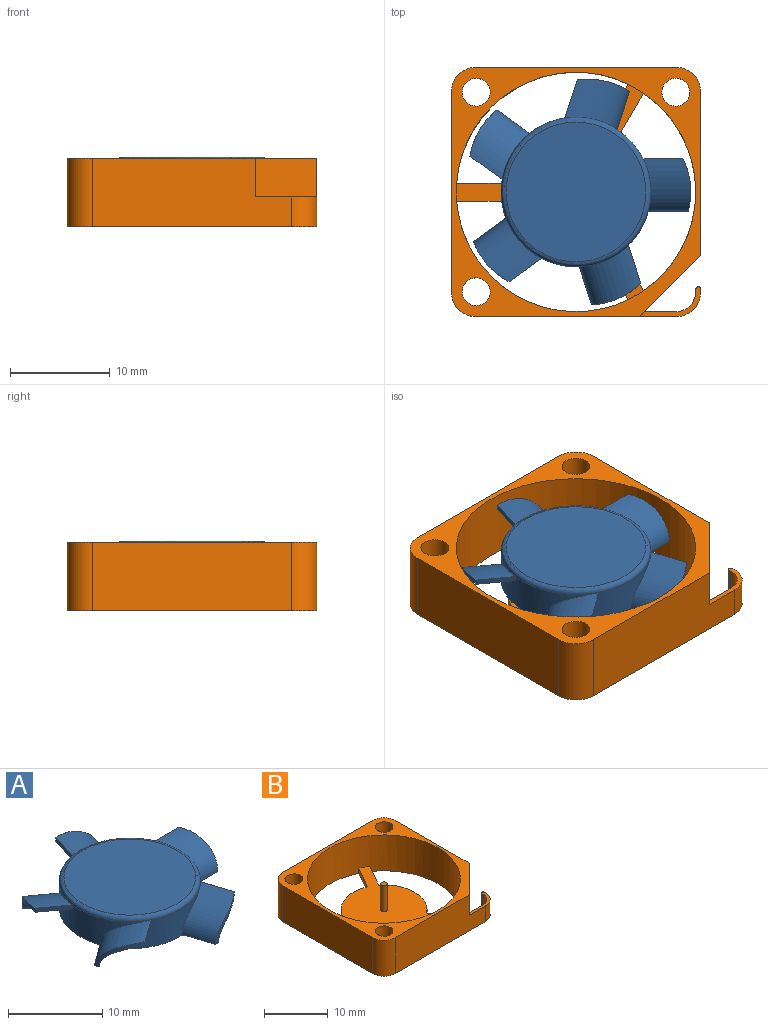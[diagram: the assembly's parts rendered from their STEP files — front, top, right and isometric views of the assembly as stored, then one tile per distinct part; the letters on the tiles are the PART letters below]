
ASSEMBLY  parts=2 mates=1
PART A: 31 faces, bbox 22.1x22.6x4 mm
  f0: cylinder r=6.5mm len=13mm, axis (0,0,-1), area 122.5mm2, adj f24,f25
  f1: torus R=7mm, axis (0,0,1), area 36.1mm2, adj f2,f23
  f2: cylinder r=7.5mm len=15mm, axis (0,0,-1), area 148.3mm2, adj f1,f3,f4,f6,f7,f8,f9,f11
  f3: plane 3.84x1.75mm, normal (0,0,-1), area 2mm2, adj f2,f5,f6,f7
  f4: plane 3.8x1.24mm, normal (0.95,0.31,0), area 2mm2, adj f2,f5,f6,f7
  f5: cylinder r=7.5mm len=4.92mm, axis (0,0,-1), area 3.3mm2, adj f3,f4,f6,f7
  f6: bspline ~5.96x5.66mm, area 24.4mm2, adj f2,f3,f4,f5
  f7: bspline ~6.16x5.94mm, area 27.6mm2, adj f2,f3,f4,f5
  f8: plane 3.43x2.83mm, normal (0,0,-1), area 2mm2, adj f2,f10,f11,f12
  f9: plane 3.24x2.35mm, normal (0.59,-0.81,0), area 2mm2, adj f2,f10,f11,f12
  f10: cylinder r=7.5mm len=4.02mm, axis (0,0,-1), area 3.3mm2, adj f8,f9,f11,f12
  f11: bspline ~6.65x5.93mm, area 24.4mm2, adj f2,f8,f9,f10
  f12: bspline ~6.79x6.37mm, area 27.6mm2, adj f2,f8,f9,f10
  f13: plane 3.63x2.69mm, normal (0,0,-1), area 2mm2, adj f2,f15,f16,f17
  f14: plane 3.24x2.35mm, normal (-0.59,-0.81,0), area 2mm2, adj f2,f15,f16,f17
  f15: cylinder r=7.5mm len=4.62mm, axis (0,0,-1), area 3.3mm2, adj f13,f14,f16,f17
  f16: bspline ~6.64x5.57mm, area 24.4mm2, adj f2,f13,f14,f15
  f17: bspline ~6.98x5.96mm, area 27.6mm2, adj f2,f13,f14,f15
  f18: plane 4.07x1.67mm, normal (0,0,-1), area 2mm2, adj f2,f20,f21,f22
  f19: plane 3.8x1.24mm, normal (-0.95,0.31,0), area 2mm2, adj f2,f20,f21,f22
  f20: cylinder r=7.5mm len=5.24mm, axis (0,0,-1), area 3.3mm2, adj f18,f19,f21,f22
  f21: bspline ~6.04x4.78mm, area 24.4mm2, adj f2,f18,f19,f20
  f22: bspline ~6.48x5.07mm, area 27.6mm2, adj f2,f18,f19,f20
  f23: plane 14x14mm, normal (0,0,1), area 153.9mm2, adj f1
  f24: plane 15x15mm, normal (0,0,-1), area 44mm2, adj f0,f2
  f25: plane 13x13mm, normal (0,0,-1), area 132.7mm2, adj f0
  f26: bspline ~5.34x4.79mm, area 27.6mm2, adj f2,f28,f29,f30
  f27: bspline ~4.84x4.82mm, area 24.4mm2, adj f2,f28,f29,f30
  f28: plane 4x0.5mm, normal (0,1,0), area 2mm2, adj f2,f26,f27,f30
  f29: plane 4.12x0.5mm, normal (0,0,-1), area 2mm2, adj f2,f26,f27,f30
  f30: cylinder r=7.5mm len=5.34mm, axis (0,0,-1), area 3.3mm2, adj f26,f27,f28,f29
PART B: 33 faces, bbox 25x25x6.9 mm
  f0: cylinder r=0.5mm len=5mm, axis (0,0,-1), area 15.7mm2, adj f7,f32
  f1: cylinder r=6.75mm len=9.26mm, axis (0,0,-1), area 12.3mm2, adj f7,f10,f30,f31
  f2: cylinder r=0.25mm len=3mm, axis (0,0,-1), area 2.4mm2, adj f10,f19,f21,f22
  f3: cylinder r=1.4mm len=6.9mm, axis (0,0,-1), area 60.7mm2, adj f9,f10
  f4: cylinder r=1.4mm len=6.9mm, axis (0,0,-1), area 60.7mm2, adj f9,f10
  f5: cylinder r=1.4mm len=6.9mm, axis (0,0,-1), area 60.7mm2, adj f9,f10
  f6: cylinder r=12mm len=24mm, axis (0,0,-1), area 514.8mm2, adj f7,f9,f10,f24,f26,f27,f29,f30
  f7: plane 21.63x18.76mm, normal (0,0,1), area 170.8mm2, adj f0,f1,f6,f24,f25,f26,f27,f28
  f8: plane 6.9x6.12mm, normal (0.71,-0.71,0), area 57.6mm2, adj f9,f10,f12,f13,f18,f19
  f9: plane 25x25mm, normal (0,0,1), area 131.4mm2, adj f3,f4,f5,f6,f8,f11,f12,f13
  f10: plane 25x25mm, normal (0,0,-1), area 306.6mm2, adj f1,f2,f3,f4,f5,f6,f8,f11
  f11: cylinder r=2.5mm len=6.9mm, axis (0,0,-1), area 27.1mm2, adj f9,f10,f12,f17
  f12: plane 20x6.9mm, normal (0,-1,0), area 123.9mm2, adj f8,f9,f10,f11,f19,f20
  f13: plane 16.38x6.9mm, normal (1,0,0), area 113mm2, adj f8,f9,f10,f14
  f14: cylinder r=2.5mm len=6.9mm, axis (0,0,-1), area 27.1mm2, adj f9,f10,f13,f15
  f15: plane 20x6.9mm, normal (0,1,0), area 138mm2, adj f9,f10,f14,f16
  f16: cylinder r=2.5mm len=6.9mm, axis (0,0,-1), area 27.1mm2, adj f9,f10,f15,f17
  f17: plane 20x6.9mm, normal (-1,0,0), area 138mm2, adj f9,f10,f11,f16
  f18: plane 3.12x3mm, normal (0,1,0), area 9.4mm2, adj f8,f10,f19,f23
  f19: plane 6.12x3mm, normal (0,0,1), area 3.7mm2, adj f2,f8,f12,f18,f20,f21,f22,f23
  f20: cylinder r=2.5mm len=3mm, axis (0,0,-1), area 11.8mm2, adj f10,f12,f19,f21
  f21: plane 3x0.25mm, normal (1,0,0), area 0.8mm2, adj f2,f10,f19,f20
  f22: plane 3x0.25mm, normal (-1,0,0), area 0.8mm2, adj f2,f10,f19,f23
  f23: cylinder r=2mm len=3mm, axis (0,0,-1), area 9.4mm2, adj f10,f18,f19,f22
  f24: plane 5.28x1mm, normal (0,-1,0), area 5.3mm2, adj f6,f7,f10,f25
  f25: cylinder r=6.75mm len=9.26mm, axis (0,0,-1), area 12.3mm2, adj f7,f10,f24,f26
  f26: plane 4.57x2.64mm, normal (-0.87,-0.5,0), area 5.3mm2, adj f6,f7,f10,f25
  f27: plane 4.57x2.64mm, normal (0.87,0.5,0), area 5.3mm2, adj f6,f7,f10,f28
  f28: cylinder r=6.75mm len=10.69mm, axis (0,0,-1), area 12.3mm2, adj f7,f10,f27,f29
  f29: plane 4.57x2.64mm, normal (0.87,-0.5,0), area 5.3mm2, adj f6,f7,f10,f28
  f30: plane 4.57x2.64mm, normal (-0.87,0.5,0), area 5.3mm2, adj f1,f6,f7,f10
  f31: plane 5.28x1mm, normal (0,1,0), area 5.3mm2, adj f1,f6,f7,f10
  f32: plane 1x1mm, normal (0,0,1), area 0.8mm2, adj f0
PLACE A t=(1.98,-16.68,10.64)mm
PLACE B t=(1.98,-16.68,7.64)mm
MATE revolute A.f0 <-> B.f0  axis (0,0,-1) through (1.98,-16.68,13.64)mm
